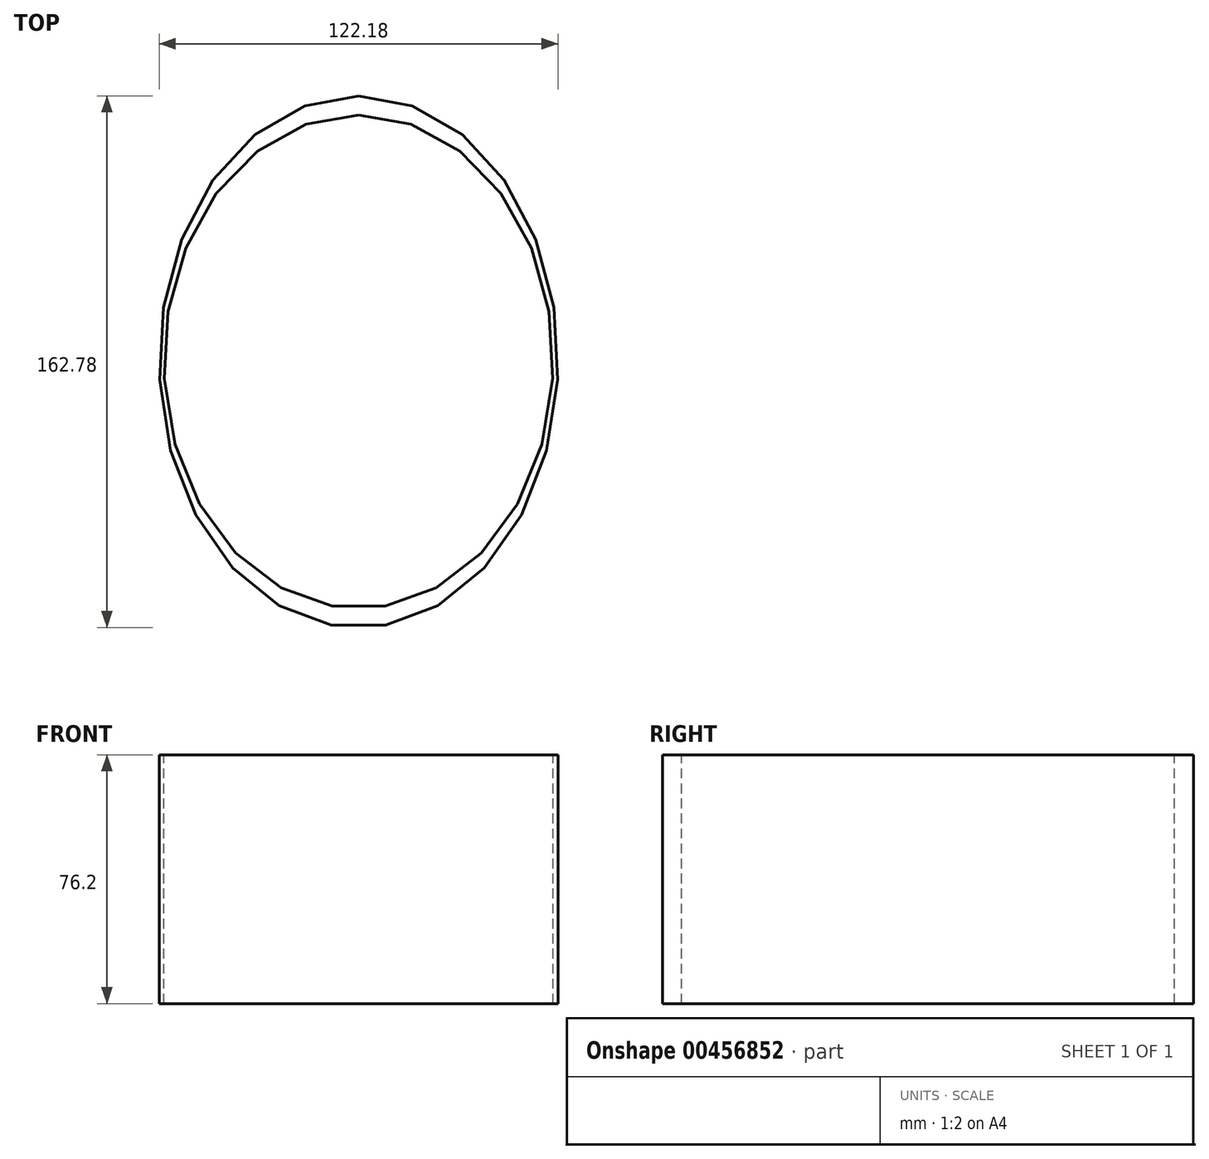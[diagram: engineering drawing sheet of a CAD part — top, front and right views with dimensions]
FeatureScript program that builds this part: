
annotation { "Feature Type Name" : "Feature", "Feature Type Description" : "" }
export const myFeature = defineFeature(function(context is Context, id is Id, definition is map)
    precondition{}
    {
        {
            var Q0;
            Q0=qCreatedBy(makeId("Top.planeOp"),FACE);
            var sketch = newSketch(context, id + "F0", { "sketchPlane" : qUnion([Q0])});
            skEllipse(sketch, "E0", {"center": v(0, 0) * mm, "majorRadius": 59.64 * mm, "minorRadius": 75.5 * mm, "majorAxis": v(1, 0)});
            skSolve(sketch);
        }
        {
            var Q0;
            Q0=qCreatedBy(makeId("Top.planeOp"),FACE);
            var sketch = newSketch(context, id + "F1", { "sketchPlane" : qUnion([Q0])});
            skEllipse(sketch, "E1", {"center": v(0, 0) * mm, "majorRadius": 61.1 * mm, "minorRadius": 81.4 * mm, "majorAxis": v(1, 0)});
            skSolve(sketch);
        }
        {
            var Q0;
            Q0=sQuery(id+"F0.wireOp",EDGE,"E0");
            extrude(context, id + "F2", {"bodyType" : ToolBodyType.SURFACE, "surfaceEntities" : qUnion([Q0]), "depth" : 76.2 * mm});
        }
        {
            var Q0;
            Q0=makeQuery(id+"F0.imprint","IMPRINT",FACE,{"disambiguationData":[TD([[makeQuery(id+"F0.imprint","IMPRINT",EDGE,{"derivedFrom":sQuery(id+"F0.wireOp",EDGE,"E0")}),1.0]])]});
            extrude(context, id + "F3", {"entities" : qUnion([Q0]), "depth" : 76.2 * mm});
        }
        {
            var Q0;
            Q0=makeQuery(id+"F3.opExtrude","SWEPT_BODY",BODY,{"disambiguationData":[OSD([sQuery(id+"F0.wireOp",EDGE,"E0")])]});
            deleteBodies(context, id + "F4", {"entities" : qUnion([Q0])});
        }
        {
            var Q0;
            Q0=sQuery(id+"F1.wireOp",EDGE,"E1");
            extrude(context, id + "F5", {"bodyType" : ToolBodyType.SURFACE, "surfaceEntities" : qUnion([Q0]), "depth" : 76.2 * mm});
        }
    });
